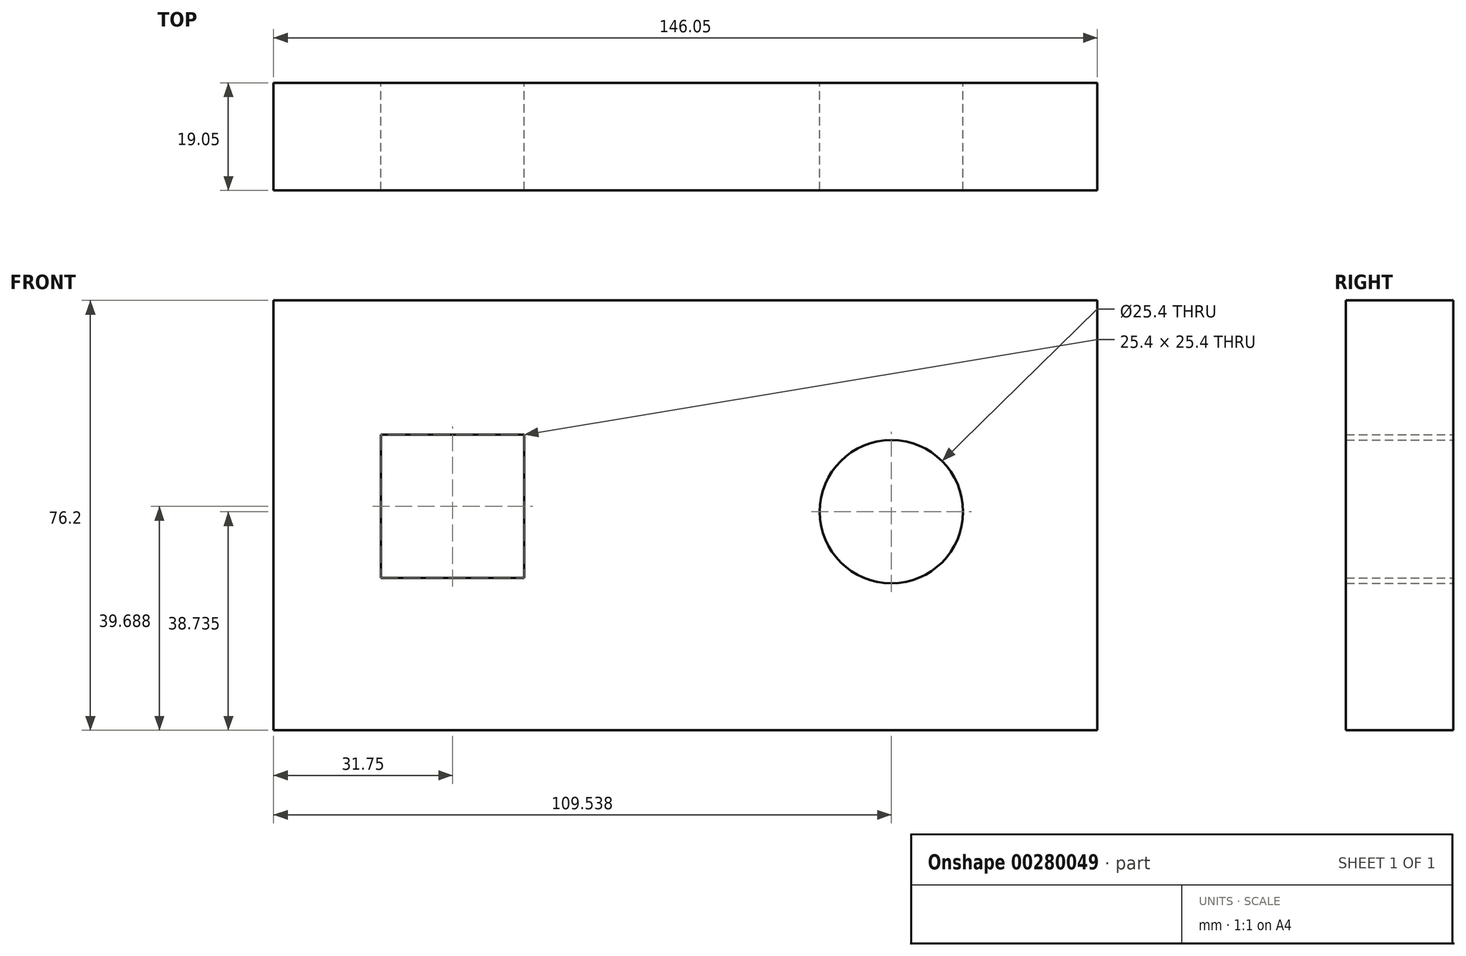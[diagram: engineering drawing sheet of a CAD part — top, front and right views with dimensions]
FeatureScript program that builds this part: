
annotation { "Feature Type Name" : "Feature", "Feature Type Description" : "" }
export const myFeature = defineFeature(function(context is Context, id is Id, definition is map)
    precondition{}
    {
        {
            var Q0;
            Q0=qCreatedBy(makeId("Front.planeOp"),FACE);
            var sketch = newSketch(context, id + "F0", { "sketchPlane" : qUnion([Q0])});
            skLineSegment(sketch, "E0.bottom", {"start": v(0, 0) * mm, "end": v(-146.05, 0) * mm});
            skLineSegment(sketch, "E0.top", {"start": v(0, 76.2) * mm, "end": v(-146.05, 76.2) * mm});
            skLineSegment(sketch, "E0.left", {"start": v(0, 0) * mm, "end": v(0, 76.2) * mm});
            skLineSegment(sketch, "E0.right", {"start": v(-146.05, 0) * mm, "end": v(-146.05, 76.2) * mm});
            skLineSegment(sketch, "E1.bottom", {"start": v(-127, 52.39) * mm, "end": v(-101.6, 52.39) * mm});
            skLineSegment(sketch, "E1.top", {"start": v(-127, 26.99) * mm, "end": v(-101.6, 26.99) * mm});
            skLineSegment(sketch, "E1.left", {"start": v(-127, 52.39) * mm, "end": v(-127, 26.99) * mm});
            skLineSegment(sketch, "E1.right", {"start": v(-101.6, 52.39) * mm, "end": v(-101.6, 26.99) * mm});
            skCircle(sketch, "E2", {"center": v(-36.51, 38.73) * mm, "radius": 12.7 * mm});
            skSolve(sketch);
        }
        {
            var Q0;
            Q0=makeQuery(id+"F0.imprint","IMPRINT",FACE,{"disambiguationData":[TD([[makeQuery(id+"F0.imprint","IMPRINT",EDGE,{"derivedFrom":sQuery(id+"F0.wireOp",EDGE,"E0.bottom")}),-1.0]])]});
            extrude(context, id + "F1", {"entities" : qUnion([Q0]), "depth" : 19.05 * mm});
        }
    });
